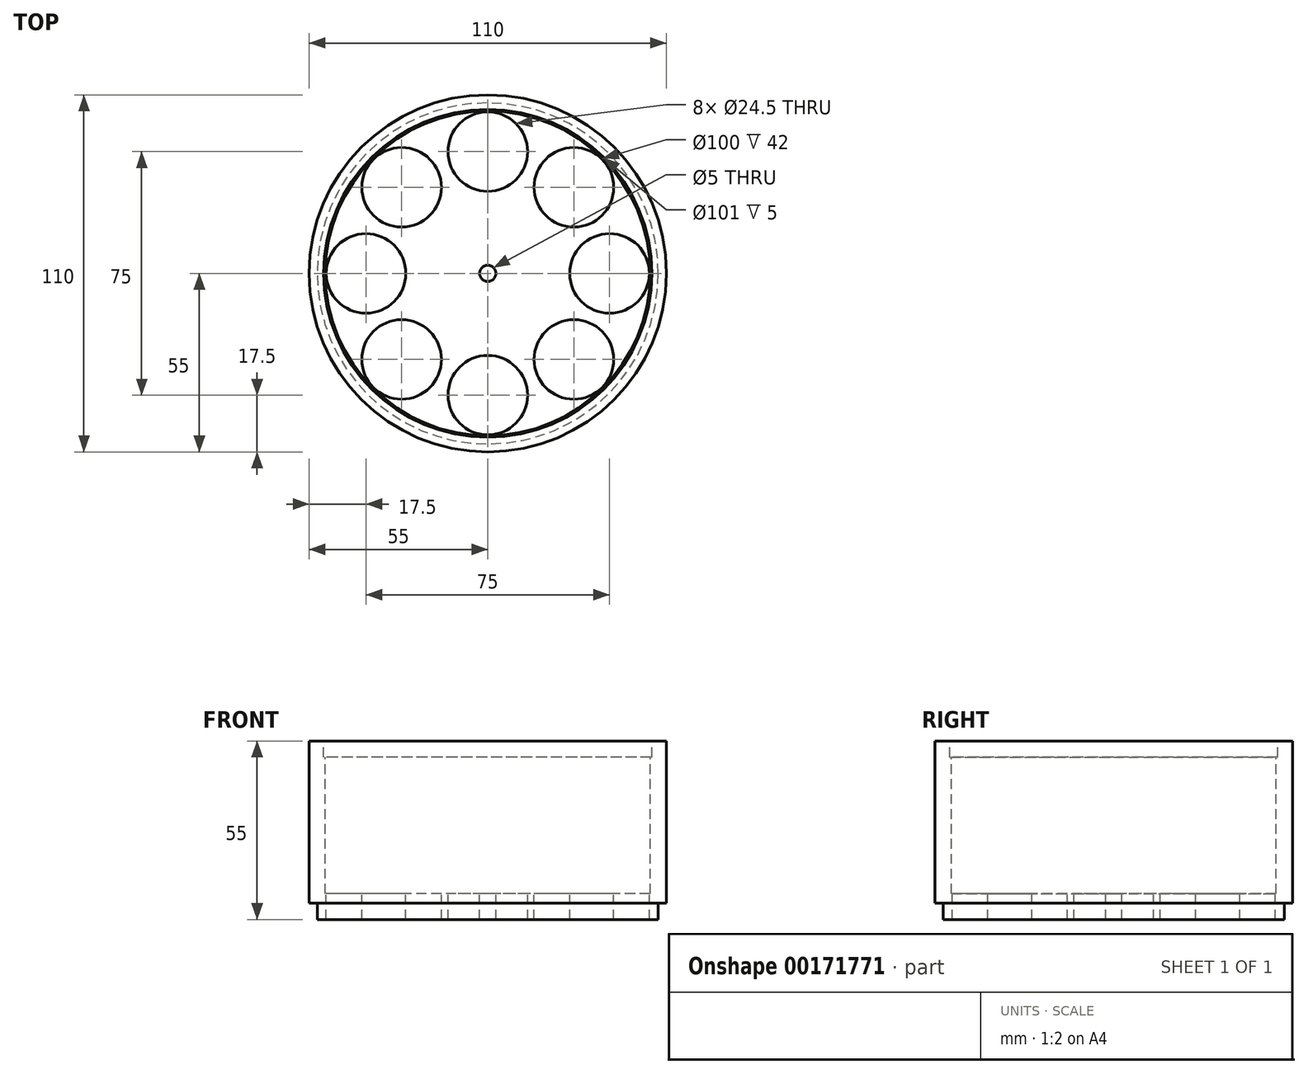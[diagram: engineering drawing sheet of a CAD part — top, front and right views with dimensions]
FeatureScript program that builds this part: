
annotation { "Feature Type Name" : "Feature", "Feature Type Description" : "" }
export const myFeature = defineFeature(function(context is Context, id is Id, definition is map)
    precondition{}
    {
        {
            var Q0;
            Q0=qCreatedBy(makeId("Top.planeOp"),FACE);
            var sketch = newSketch(context, id + "F0", { "sketchPlane" : qUnion([Q0])});
            skCircle(sketch, "E0", {"center": v(0, 0) * mm, "radius": 55 * mm});
            skCircle(sketch, "E1", {"center": v(0, 0) * mm, "radius": 52.5 * mm});
            skCircle(sketch, "E2", {"center": v(0, 0) * mm, "radius": 2.5 * mm});
            skSolve(sketch);
        }
        {
            var Q0;
            Q0=makeQuery(id+"F0.imprint","IMPRINT",FACE,{"disambiguationData":[TD([[makeQuery(id+"F0.imprint","IMPRINT",EDGE,{"derivedFrom":sQuery(id+"F0.wireOp",EDGE,"E1")}),1.0]])]});
            extrude(context, id + "F1", {"entities" : qUnion([Q0]), "oppositeDirection" : true, "depth" : 5 * mm});
        }
        {
            var Q0;
            Q0 = qSketchRegion(id + "F0", true);
            var Q1;
            Q1=makeQuery(id+"F1.opExtrude","CAP_FACE",FACE,{"disambiguationData":[OSD([sQuery(id+"F0.wireOp",EDGE,"E1"),sQuery(id+"F0.wireOp",EDGE,"E2")])],"isStart":true});
            extrude(context, id + "F2", {"entities" : qUnion([Q0, Q1]), "operationType" : NewBodyOperationType.ADD, "depth" : 50 * mm});
        }
        {
            var Q0;
            {var subQ0=sQuery(id+"F0.wireOp",EDGE,"E1");Q0=makeQuery(id+"F2.boolean.opBoolean","MERGE",FACE,{"derivedFrom":[makeQuery(id+"F2.opExtrude","CAP_FACE",FACE,{"disambiguationData":[OSD([sQuery(id+"F0.wireOp",EDGE,"E0"),subQ0])],"isStart":false}),makeQuery(id+"F2.opExtrude","CAP_FACE",FACE,{"disambiguationData":[OSD([subQ0,sQuery(id+"F0.wireOp",EDGE,"E2")])],"isStart":false})]});}
            var sketch = newSketch(context, id + "F3", { "sketchPlane" : qUnion([Q0])});
            skCircle(sketch, "E3", {"center": v(0, 0) * mm, "radius": 50 * mm});
            skSolve(sketch);
        }
        {
            var Q0;
            Q0=makeQuery(id+"F3.imprint","IMPRINT",FACE,{"disambiguationData":[TD([[makeQuery(id+"F3.imprint","IMPRINT",EDGE,{"derivedFrom":sQuery(id+"F3.wireOp",EDGE,"E3")}),1.0]])]});
            extrude(context, id + "F4", {"entities" : qUnion([Q0]), "operationType" : NewBodyOperationType.REMOVE, "oppositeDirection" : true, "depth" : 47 * mm});
        }
        {
            var Q0;
            Q0=makeQuery(id+"F4.boolean.opBoolean","COPY",FACE,{"derivedFrom":makeQuery(id+"F4.opExtrude","CAP_FACE",FACE,{"disambiguationData":[OSD([sQuery(id+"F0.wireOp",EDGE,"E2"),sQuery(id+"F3.wireOp",EDGE,"E3")])],"isStart":false})});
            var sketch = newSketch(context, id + "F5", { "sketchPlane" : qUnion([Q0])});
            skLineSegment(sketch, "E4", {"start": v(0, 0) * mm, "end": v(0, 37.5) * mm});
            skCircle(sketch, "E5", {"center": v(0, 37.5) * mm, "radius": 12.25 * mm});
            skCircle(sketch, "E6.1.0", {"center": v(-26.52, 26.52) * mm, "radius": 12.25 * mm});
            skCircle(sketch, "E6.2.0", {"center": v(-37.5, 0) * mm, "radius": 12.25 * mm});
            skPoint(sketch, "E6.center", {"position": v(0, 0) * mm});
            skCircle(sketch, "E7.1.3.0", {"center": v(-26.52, -26.52) * mm, "radius": 12.25 * mm});
            skCircle(sketch, "E7.1.4.0", {"center": v(0, -37.5) * mm, "radius": 12.25 * mm});
            skCircle(sketch, "E7.1.5.0", {"center": v(26.52, -26.52) * mm, "radius": 12.25 * mm});
            skCircle(sketch, "E8.1.6.0", {"center": v(37.5, 0) * mm, "radius": 12.25 * mm});
            skCircle(sketch, "E8.1.7.0", {"center": v(26.52, 26.52) * mm, "radius": 12.25 * mm});
            skSolve(sketch);
        }
        {
            var Q0;
            Q0=makeQuery(id+"F5.imprint","IMPRINT",FACE,{"disambiguationData":[TD([[makeQuery(id+"F5.imprint","IMPRINT",EDGE,{"derivedFrom":sQuery(id+"F5.wireOp",EDGE,"E5")}),1.0]])]});
            var Q1;
            Q1=makeQuery(id+"F5.imprint","IMPRINT",FACE,{"disambiguationData":[TD([[makeQuery(id+"F5.imprint","IMPRINT",EDGE,{"derivedFrom":sQuery(id+"F5.wireOp",EDGE,"E6.1.0")}),1.0]])]});
            var Q2;
            Q2=makeQuery(id+"F5.imprint","IMPRINT",FACE,{"disambiguationData":[TD([[makeQuery(id+"F5.imprint","IMPRINT",EDGE,{"derivedFrom":sQuery(id+"F5.wireOp",EDGE,"E6.2.0")}),1.0]])]});
            var Q3;
            Q3=makeQuery(id+"F5.imprint","IMPRINT",FACE,{"disambiguationData":[TD([[makeQuery(id+"F5.imprint","IMPRINT",EDGE,{"derivedFrom":sQuery(id+"F5.wireOp",EDGE,"E7.1.3.0")}),1.0]])]});
            var Q4;
            Q4=makeQuery(id+"F5.imprint","IMPRINT",FACE,{"disambiguationData":[TD([[makeQuery(id+"F5.imprint","IMPRINT",EDGE,{"derivedFrom":sQuery(id+"F5.wireOp",EDGE,"E7.1.4.0")}),1.0]])]});
            var Q5;
            Q5=makeQuery(id+"F5.imprint","IMPRINT",FACE,{"disambiguationData":[TD([[makeQuery(id+"F5.imprint","IMPRINT",EDGE,{"derivedFrom":sQuery(id+"F5.wireOp",EDGE,"E7.1.5.0")}),1.0]])]});
            var Q6;
            Q6=makeQuery(id+"F5.imprint","IMPRINT",FACE,{"disambiguationData":[TD([[makeQuery(id+"F5.imprint","IMPRINT",EDGE,{"derivedFrom":sQuery(id+"F5.wireOp",EDGE,"E8.1.7.0")}),1.0]])]});
            var Q7;
            Q7=makeQuery(id+"F5.imprint","IMPRINT",FACE,{"disambiguationData":[TD([[makeQuery(id+"F5.imprint","IMPRINT",EDGE,{"derivedFrom":sQuery(id+"F5.wireOp",EDGE,"E8.1.6.0")}),1.0]])]});
            extrude(context, id + "F6", {"entities" : qUnion([Q0, Q1, Q2, Q3, Q4, Q5, Q6, Q7]), "operationType" : NewBodyOperationType.REMOVE, "oppositeDirection" : true, "depth" : 8 * mm});
        }
        {
            var Q0;
            {var subQ0=sQuery(id+"F0.wireOp",EDGE,"E1");Q0=makeQuery(id+"F2.boolean.opBoolean","MERGE",FACE,{"derivedFrom":[makeQuery(id+"F2.opExtrude","CAP_FACE",FACE,{"disambiguationData":[OSD([sQuery(id+"F0.wireOp",EDGE,"E0"),subQ0])],"isStart":false}),makeQuery(id+"F2.opExtrude","CAP_FACE",FACE,{"disambiguationData":[OSD([subQ0,sQuery(id+"F0.wireOp",EDGE,"E2")])],"isStart":false})]});}
            var sketch = newSketch(context, id + "F7", { "sketchPlane" : qUnion([Q0])});
            skCircle(sketch, "E9", {"center": v(0, 0) * mm, "radius": 50.5 * mm});
            skSolve(sketch);
        }
        {
            var Q0;
            Q0=makeQuery(id+"F7.imprint","IMPRINT",FACE,{"disambiguationData":[TD([[makeQuery(id+"F7.imprint","IMPRINT",EDGE,{"derivedFrom":sQuery(id+"F7.wireOp",EDGE,"E9")}),1.0]])]});
            extrude(context, id + "F8", {"entities" : qUnion([Q0]), "operationType" : NewBodyOperationType.REMOVE, "oppositeDirection" : true, "depth" : 5 * mm});
        }
    });
